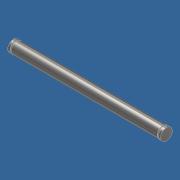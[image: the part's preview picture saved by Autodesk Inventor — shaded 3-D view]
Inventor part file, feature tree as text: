
AUTODESK INVENTOR PART (.ipt)
format: ipt  version: 2018 (Build 220112000, 112)  size: 136,704 bytes
history: native  units: mm
features: extrude x2, sketch x2, revolve x1, plane x1
ambient origin geometry x8: Origin, YZ Plane, XZ Plane, XY Plane, X Axis, Y Axis, Z Axis, Center Point
bodies: Solid1 (feature_tree)
feature tree (6):
  extrude  "Extrusion1"  Depth=105.0mm TaperAngle=0.0deg
  revolve  "Revolution1"  [1 undecoded]
  plane  "Work Plane1"
  extrude  "Extrusion4"  Depth=2.0mm
  sketch  "Sketch2"  dims[d0=8.0mm d1=105.0mm d2=0.0mm]
  sketch  "Sketch5"  dims[d9=1.5mm d10=0.94mm d11=0.5mm d12=3.0mm d13=90.0deg d18=8.0mm d19=2.0mm d20=8.0mm d21=3.0mm d22=32.0mm d23=18.0mm d24=20.0mm d25=2.0mm d26=24.5mm d27=18.0mm d28=1.2mm d29=0.0mm]
note: 1 required parameter value undecoded (feature->parameter linkage not recoverable at this tier; creation-order binding heuristic only, values carry confidence <= 0.55)
